# Revit family: RJ45 UTP_ENG
name_source: partatom
category: Equipement spécialisé
units: mm (PartAtom-declared; Revit-internal decimal feet)

## family parameters
Basée sur le plan de construction = Non
Cote de connecteur circulaire = Utiliser le diamètre
Couper avec des vides une fois chargée = Non
Partagée = Oui
Point de calcul de pièce = Non
Toujours verticalement = Oui
Type d'élément = Normal

## types (3) — shared parameters
Blindé = Non
Classe ETIM = EC001121
Diamètre max du câble en entrée = 9MM
Fonction = Prises murales RJ45
Hauteur = 31 mm  [stored 0.101706 ft]
IK = IK04
IP = IP20
Largeur (mm) = 18 mm  [stored 0.0590551 ft]
Lien e-catalogue = https://www.legrand.fr
Profondeur = 34 mm
Section AWG = 23-26
Température de fonctionnement = -10_à_60
Température de stockage = -10_à_70
Type de connecteur = RJ45
zero-valued in all types: Elévation par défaut

## per-type parameters (varying)
| type | Catégorie | Couleur | EAN | Référence Legrand | Vide |
| Connecteur RJ45 Catégorie 6A UTP (lot de 24) | 6A | IDS_ARGENT | 3414972227230 | 632906 | 2 mm  [stored 0.00656168 ft] |
| Connecteur RJ45 Catégorie 6 UTP (lot de 24) | 6 | IDS_GRIS | 3414972227292 | 632909 | 0 mm  [stored 0 ft] |
| Connecteur RJ45 Catégorie 5e UTP (lot de 24) | 5e | IDS_GRIS | 3414972227339 | 632911 | 0 mm  [stored 0 ft] |

note: column(s) folded — value = type name in every type: Libellé BIM

note: [stored X ft] marks values corroborated as IEEE doubles in the binary element streams (Revit-internal decimal feet)
